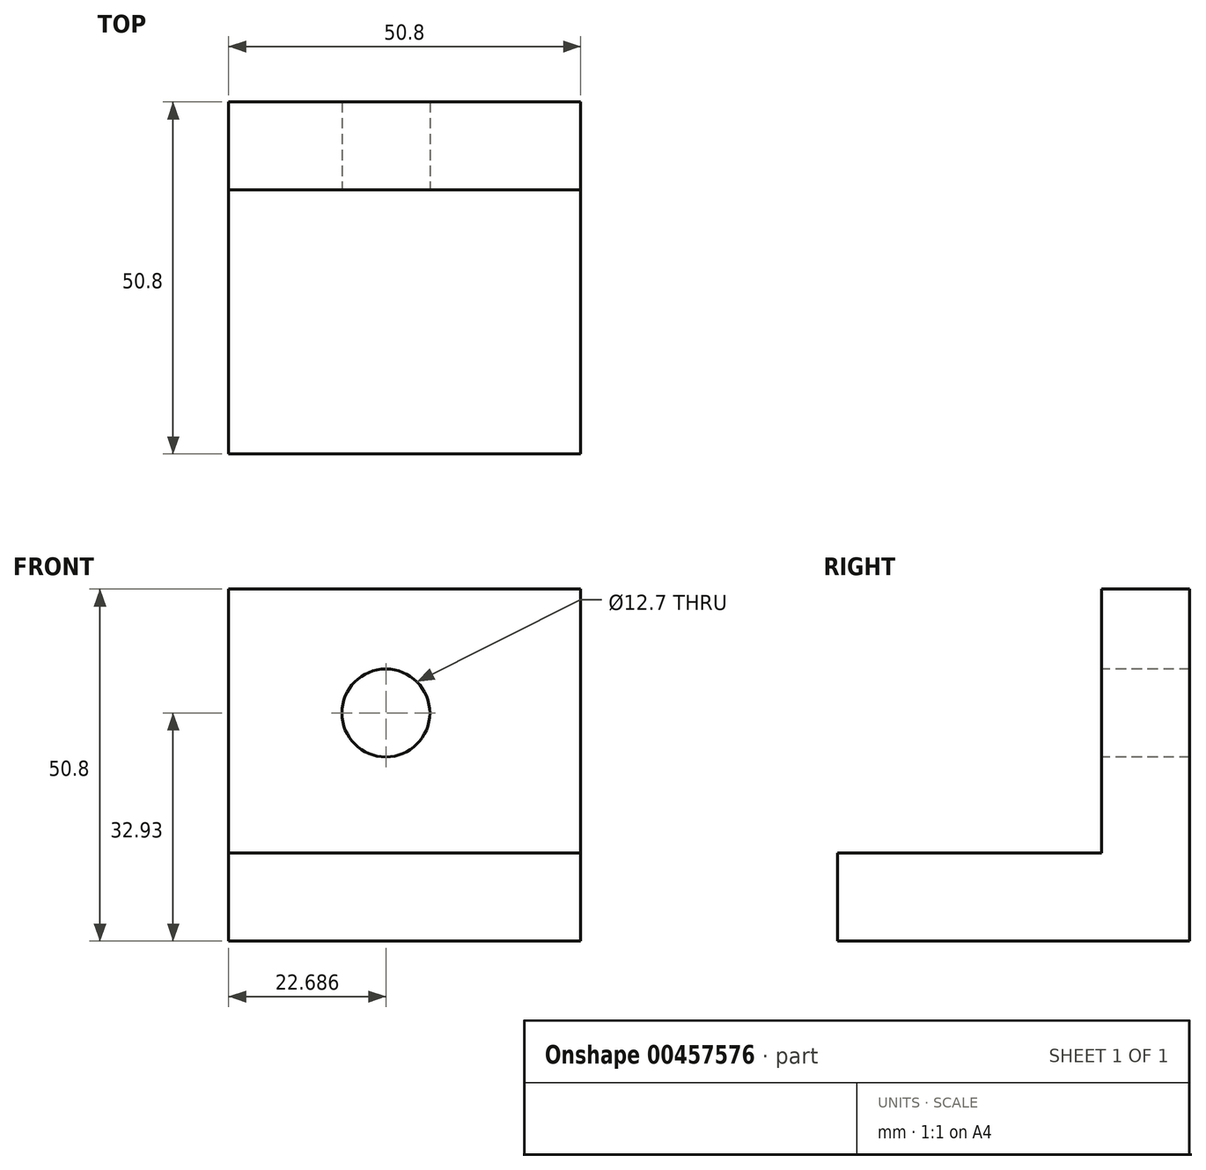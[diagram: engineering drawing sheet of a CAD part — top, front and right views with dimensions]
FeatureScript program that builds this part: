
annotation { "Feature Type Name" : "Feature", "Feature Type Description" : "" }
export const myFeature = defineFeature(function(context is Context, id is Id, definition is map)
    precondition{}
    {
        {
            var Q0;
            Q0=qCreatedBy(makeId("Top.planeOp"),FACE);
            var sketch = newSketch(context, id + "F0", { "sketchPlane" : qUnion([Q0])});
            skLineSegment(sketch, "E0.bottom", {"start": v(-55.82, -25.67) * mm, "end": v(-5.02, -25.67) * mm});
            skLineSegment(sketch, "E0.top", {"start": v(-55.82, 25.13) * mm, "end": v(-5.02, 25.13) * mm});
            skLineSegment(sketch, "E0.left", {"start": v(-55.82, -25.67) * mm, "end": v(-55.82, 25.13) * mm});
            skLineSegment(sketch, "E0.right", {"start": v(-5.02, -25.67) * mm, "end": v(-5.02, 25.13) * mm});
            skLineSegment(sketch, "E1", {"start": v(-55.82, 12.43) * mm, "end": v(-5.02, 12.43) * mm});
            skLineSegment(sketch, "E2", {"start": v(-5.02, 12.43) * mm, "end": v(-5.02, 25.13) * mm});
            skLineSegment(sketch, "E3", {"start": v(-55.82, 25.13) * mm, "end": v(-55.82, 12.43) * mm});
            skSolve(sketch);
        }
        {
            var Q0;
            Q0=makeQuery(id+"F0.imprint","IMPRINT",FACE,{"disambiguationData":[TD([[makeQuery(id+"F0.imprint","IMPRINT",EDGE,{"derivedFrom":sQuery(id+"F0.wireOp",EDGE,"E0.bottom")}),1.0]])]});
            extrude(context, id + "F1", {"entities" : qUnion([Q0]), "depth" : 12.7 * mm});
        }
        {
            var Q0;
            Q0=makeQuery(id+"F0.imprint","IMPRINT",FACE,{"disambiguationData":[TD([[makeQuery(id+"F0.imprint","IMPRINT",EDGE,{"derivedFrom":sQuery(id+"F0.wireOp",EDGE,"E0.top")}),-1.0]])]});
            extrude(context, id + "F2", {"entities" : qUnion([Q0]), "operationType" : NewBodyOperationType.ADD, "depth" : 50.8 * mm});
        }
        {
            var Q0;
            Q0=makeQuery(id+"F2.opExtrude","SWEPT_FACE",FACE,{"disambiguationData":[OSD([sQuery(id+"F0.wireOp",EDGE,"E1")])]});
            var sketch = newSketch(context, id + "F3", { "sketchPlane" : qUnion([Q0])});
            skCircle(sketch, "E4", {"center": v(-33.13, 32.93) * mm, "radius": 6.35 * mm});
            skSolve(sketch);
        }
        {
            var Q0;
            Q0=makeQuery(id+"F3.imprint","IMPRINT",FACE,{"disambiguationData":[TD([[makeQuery(id+"F3.imprint","IMPRINT",EDGE,{"derivedFrom":sQuery(id+"F3.wireOp",EDGE,"E4")}),1.0]])]});
            extrude(context, id + "F4", {"entities" : qUnion([Q0]), "operationType" : NewBodyOperationType.REMOVE, "oppositeDirection" : true, "depth" : 12.7 * mm});
        }
    });
